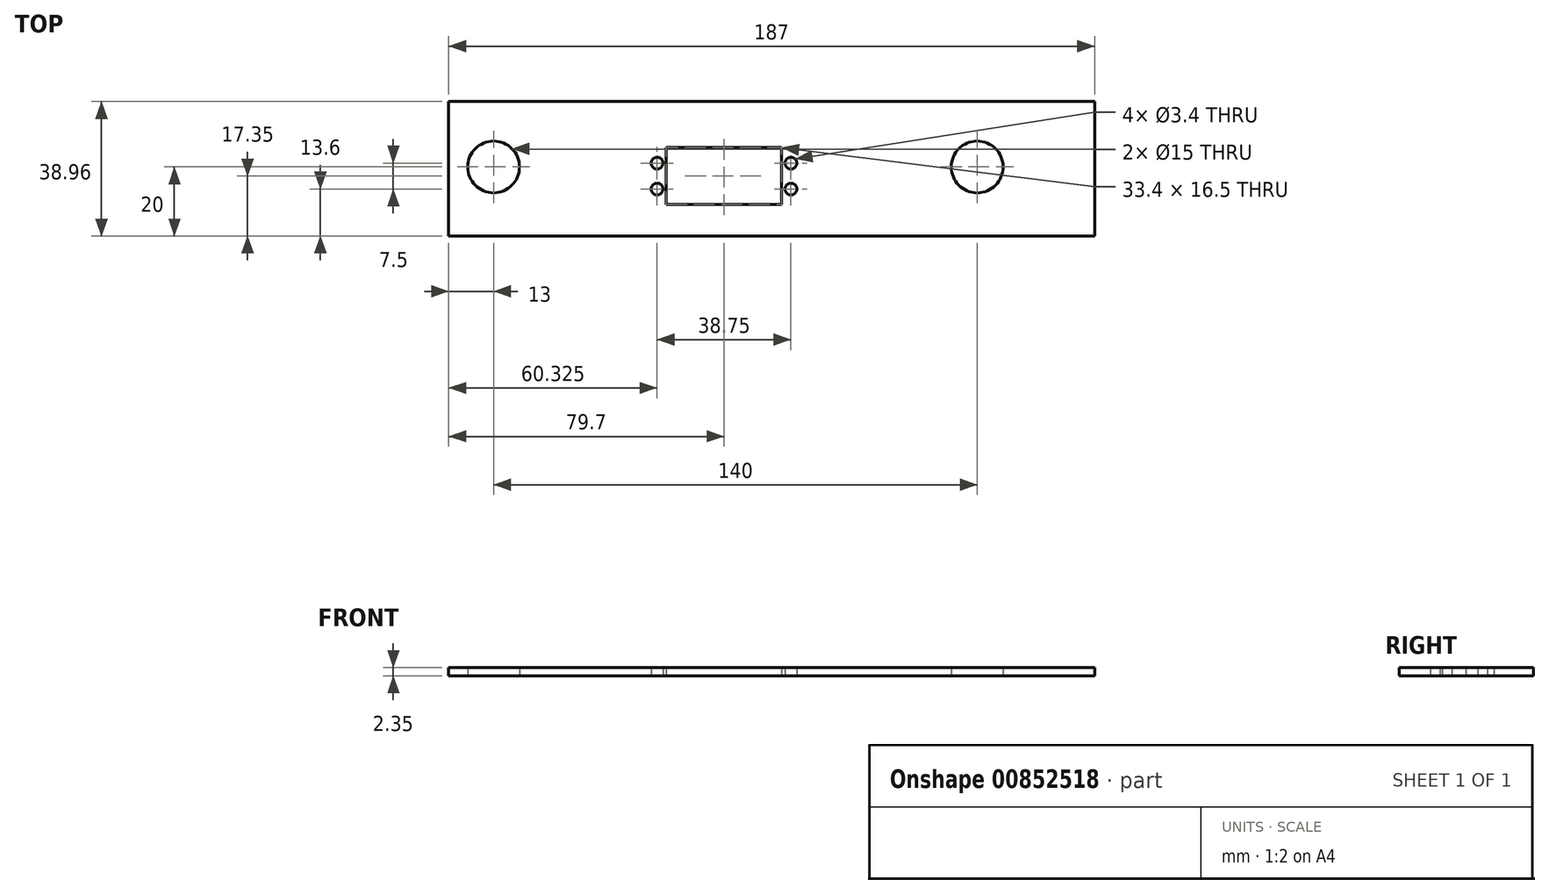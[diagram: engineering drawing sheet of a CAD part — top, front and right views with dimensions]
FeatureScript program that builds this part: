
annotation { "Feature Type Name" : "Feature", "Feature Type Description" : "" }
export const myFeature = defineFeature(function(context is Context, id is Id, definition is map)
    precondition{}
    {
        {
            var Q0;
            Q0=qCreatedBy(makeId("Top.planeOp"),FACE);
            var sketch = newSketch(context, id + "F0", { "sketchPlane" : qUnion([Q0])});
            skLineSegment(sketch, "E0.bottom", {"start": v(-20, 5.6) * mm, "end": v(13.4, 5.6) * mm});
            skLineSegment(sketch, "E0.top", {"start": v(-20, -10.9) * mm, "end": v(13.4, -10.9) * mm});
            skLineSegment(sketch, "E0.left", {"start": v(-20, 5.6) * mm, "end": v(-20, -10.9) * mm});
            skLineSegment(sketch, "E0.right", {"start": v(13.4, 5.6) * mm, "end": v(13.4, -10.9) * mm});
            skLineSegment(sketch, "E1.bottom", {"start": v(-83, 18.96) * mm, "end": v(104, 18.96) * mm});
            skLineSegment(sketch, "E1.top", {"start": v(-83, -20) * mm, "end": v(104, -20) * mm});
            skLineSegment(sketch, "E1.left", {"start": v(-83, 18.96) * mm, "end": v(-83, -20) * mm});
            skLineSegment(sketch, "E1.right", {"start": v(104, 18.96) * mm, "end": v(104, -20) * mm});
            skCircle(sketch, "E2", {"center": v(70, 0) * mm, "radius": 7.5 * mm});
            skCircle(sketch, "E3", {"center": v(-70, 0) * mm, "radius": 7.5 * mm});
            skLineSegment(sketch, "E4", {"start": v(-70, 0) * mm, "end": v(70, 0) * mm, "construction": true});
            skLineSegment(sketch, "E5", {"start": v(-20, 5.6) * mm, "end": v(13.4, -10.9) * mm, "construction": true});
            skLineSegment(sketch, "E6", {"start": v(13.4, 5.6) * mm, "end": v(-20, -10.9) * mm, "construction": true});
            skLineSegment(sketch, "E7.bottom", {"start": v(-22.68, 1.1) * mm, "end": v(16.07, 1.1) * mm, "construction": true});
            skLineSegment(sketch, "E7.top", {"start": v(-22.68, -6.4) * mm, "end": v(16.07, -6.4) * mm, "construction": true});
            skLineSegment(sketch, "E7.left", {"start": v(-22.68, 1.1) * mm, "end": v(-22.68, -6.4) * mm, "construction": true});
            skLineSegment(sketch, "E7.right", {"start": v(16.07, 1.1) * mm, "end": v(16.07, -6.4) * mm, "construction": true});
            skPoint(sketch, "E7.middle", {"position": v(-3.3, -2.65) * mm});
            skCircle(sketch, "E8", {"center": v(-22.68, 1.1) * mm, "radius": 1.7 * mm});
            skCircle(sketch, "E9", {"center": v(16.07, 1.1) * mm, "radius": 1.7 * mm});
            skCircle(sketch, "E10", {"center": v(16.07, -6.4) * mm, "radius": 1.7 * mm});
            skCircle(sketch, "E11", {"center": v(-22.68, -6.4) * mm, "radius": 1.7 * mm});
            skSolve(sketch);
        }
        {
            var Q0;
            Q0=makeQuery(id+"F0.imprint","IMPRINT",FACE,{"disambiguationData":[TD([[makeQuery(id+"F0.imprint","IMPRINT",EDGE,{"derivedFrom":sQuery(id+"F0.wireOp",EDGE,"E0.bottom")}),1.0]])]});
            extrude(context, id + "F1", {"entities" : qUnion([Q0]), "depth" : 2.35 * mm, "offsetDistance" : 25 * mm});
        }
    });
